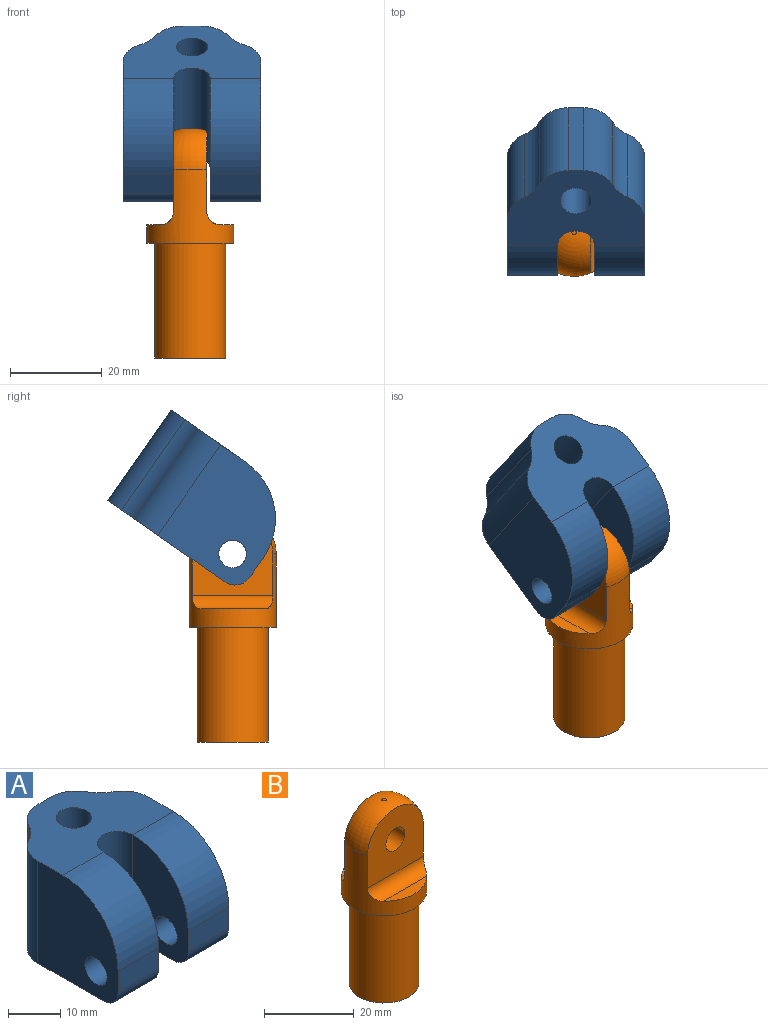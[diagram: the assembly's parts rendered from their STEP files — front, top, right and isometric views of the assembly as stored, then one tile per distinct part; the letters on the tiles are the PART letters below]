
ASSEMBLY  parts=2 mates=1
PART A: 23 faces, bbox 30x35x24 mm
  f0: plane 31x30mm, normal (0,0,-1), area 662.8mm2, adj f2,f3,f5,f7,f8,f9,f14,f15
  f1: plane 11x5mm, normal (0,-1,0), area 55mm2, adj f3,f7,f13,f21
  f2: plane 24x3.47mm, normal (0,1,0), area 83.2mm2, adj f0,f6,f16,f18
  f3: plane 24x21.73mm, normal (-1,0,0), area 441.6mm2, adj f0,f1,f6,f11,f13,f19,f21
  f4: plane 11x5mm, normal (0,-1,0), area 55mm2, adj f5,f8,f12,f20
  f5: plane 24x21.73mm, normal (1,0,0), area 441.6mm2, adj f0,f4,f6,f10,f12,f17,f20
  f6: plane 30x20mm, normal (0,0,1), area 420.8mm2, adj f2,f3,f5,f9,f12,f13,f14,f15
  f7: plane 24x15mm, normal (1,0,0), area 280mm2, adj f0,f1,f11,f13,f21,f22
  f8: plane 24x15mm, normal (-1,0,0), area 280mm2, adj f0,f4,f10,f12,f20,f22
  f9: cylinder r=3.4mm len=24mm, axis (0,0,1), area 512.7mm2, adj f0,f6
  f10: cylinder r=3mm len=11mm, axis (1,0,0), area 207.3mm2, adj f5,f8
  f11: cylinder r=3mm len=11mm, axis (1,0,0), area 207.3mm2, adj f3,f7
  f12: cylinder r=15mm len=15mm, axis (-1,0,0), area 259.2mm2, adj f4,f5,f6,f8
  f13: cylinder r=15mm len=15mm, axis (-1,0,0), area 259.2mm2, adj f1,f3,f6,f7
  f14: cylinder r=8mm len=24mm, axis (0,0,1), area 115.2mm2, adj f0,f6,f16,f17
  f15: cylinder r=8mm len=24mm, axis (0,0,1), area 115.2mm2, adj f0,f6,f18,f19
  f16: cylinder r=7mm len=24mm, axis (0,0,1), area 182.3mm2, adj f0,f2,f6,f14
  f17: cylinder r=7mm len=24mm, axis (0,0,1), area 182.3mm2, adj f0,f5,f6,f14
  f18: cylinder r=7mm len=24mm, axis (0,0,1), area 182.3mm2, adj f0,f2,f6,f15
  f19: cylinder r=7mm len=24mm, axis (0,0,1), area 182.3mm2, adj f0,f3,f6,f15
  f20: cylinder r=4mm len=11mm, axis (1,0,0), area 69.1mm2, adj f0,f4,f5,f8
  f21: cylinder r=4mm len=11mm, axis (1,0,0), area 69.1mm2, adj f0,f1,f3,f7
  f22: cylinder r=4mm len=24mm, axis (0,0,-1), area 301.6mm2, adj f0,f6,f7,f8
PART B: 15 faces, bbox 19x19x50 mm
  f0: cylinder r=9.5mm len=19mm, axis (0,0,-1), area 424.7mm2, adj f1,f3,f8,f9,f10,f11,f13,f14
  f1: torus R=0.5mm, axis (0,0,1), area 209.8mm2, adj f0,f2,f9,f11
  f2: plane 1x1mm, normal (0,0,1), area 0.8mm2, adj f1
  f3: plane 19x19mm, normal (0,0,-1), area 94.8mm2, adj f0,f5
  f4: cylinder r=4.5mm len=25mm, axis (0,0,1), area 706.9mm2, adj f6,f7
  f5: cylinder r=7.75mm len=25mm, axis (0,0,1), area 1217.4mm2, adj f3,f6
  f6: plane 15.5x15.5mm, normal (0,0,-1), area 125.1mm2, adj f4,f5
  f7: plane 9x9mm, normal (0,0,-1), area 63.6mm2, adj f4
  f8: plane 13.67x2.9mm, normal (0,0,1), area 27.3mm2, adj f0,f13
  f9: plane 17.59x17.45mm, normal (0,1,0), area 247.2mm2, adj f0,f1,f12,f13
  f10: plane 13.67x2.9mm, normal (0,0,1), area 27.3mm2, adj f0,f14
  f11: plane 17.59x17.45mm, normal (0,-1,0), area 247.2mm2, adj f0,f1,f12,f14
  f12: cylinder r=3mm len=7.2mm, axis (0,-1,0), area 135.7mm2, adj f9,f11
  f13: cylinder r=3mm len=17.58mm, axis (-1,0,0), area 73.6mm2, adj f0,f8,f9
  f14: cylinder r=3mm len=17.58mm, axis (-1,0,0), area 73.6mm2, adj f0,f10,f11
PLACE A rot(axis=(1,0,0),35deg) t=(0,-2.62,14.6)mm
PLACE B rot(axis=(0,0,-1),90deg) t=(14.6,-29.81,-13.12)mm
MATE revolute B.f12 <-> A.f10  axis (-1,0,0) through (11,-29.81,2.88)mm
